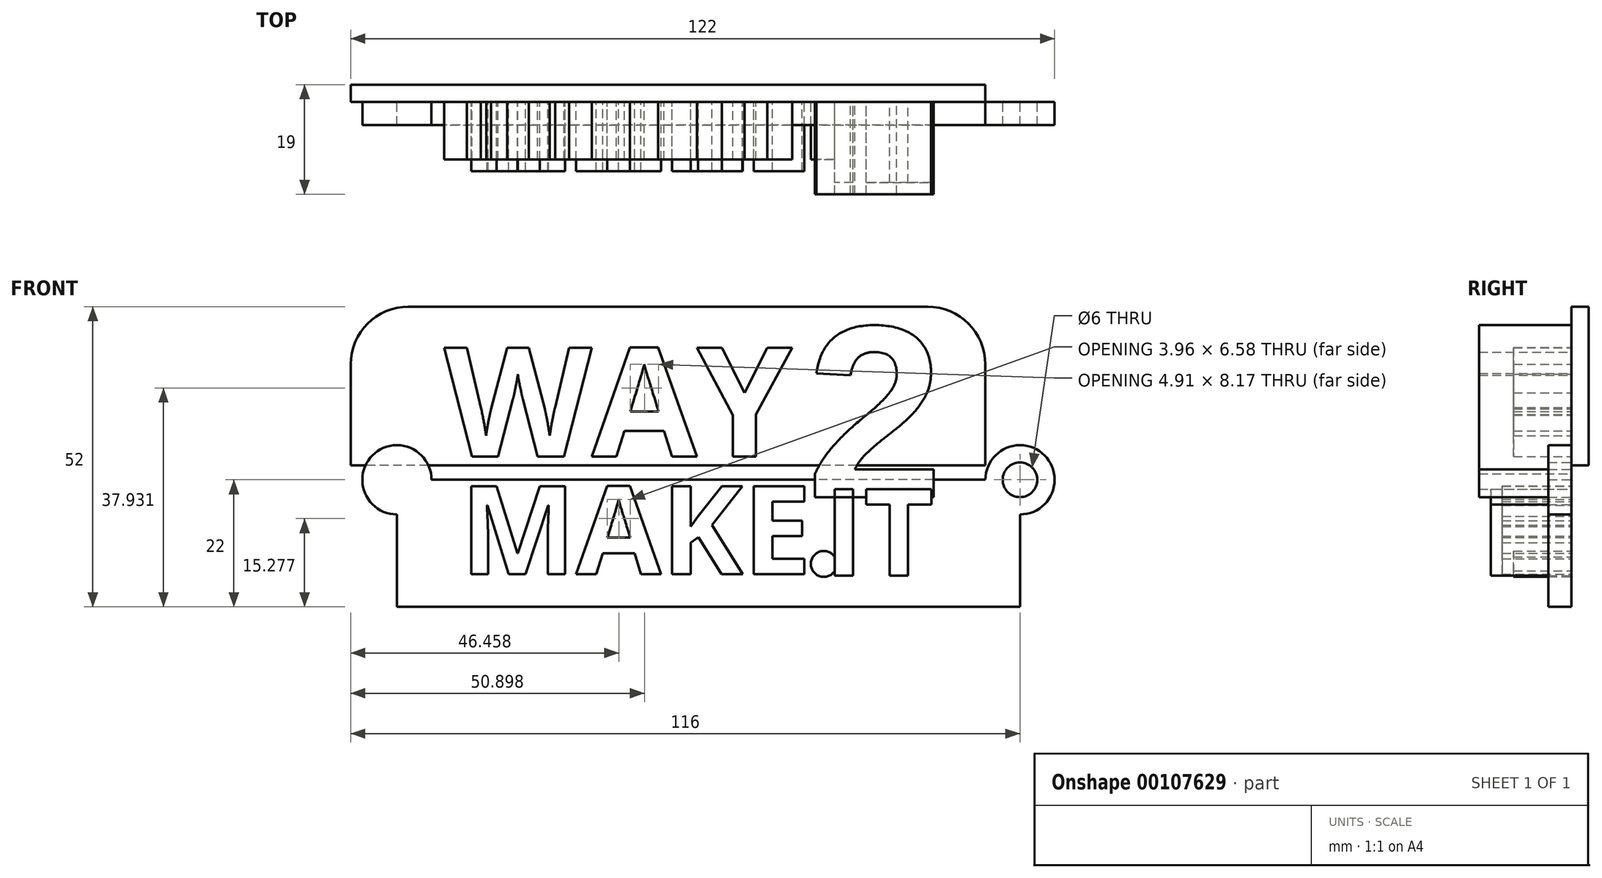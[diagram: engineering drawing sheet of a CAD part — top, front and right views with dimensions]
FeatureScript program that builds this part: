
annotation { "Feature Type Name" : "Feature", "Feature Type Description" : "" }
export const myFeature = defineFeature(function(context is Context, id is Id, definition is map)
    precondition{}
    {
        {
            var Q0;
            Q0=qCreatedBy(makeId("Front.planeOp"),FACE);
            var sketch = newSketch(context, id + "F0", { "sketchPlane" : qUnion([Q0])});
            skText(sketch, "E0", { "text": "WAY", "fontName": "OpenSans-Bold.ttf"});
            skText(sketch, "E1", { "text": "2", "fontName": "Arimo-Bold.ttf"});
            skText(sketch, "E2", { "text": "MAKE", "fontName": "OpenSans-Bold.ttf"});
            skText(sketch, "E3", { "text": "IT", "fontName": "OpenSans-Bold.ttf"});
            const initialGuessF0  = {"E0": [-0.0538, 0, 1, 0, 0.01903], "E1": [0.009, -0.007, 1, 0, 0.03074], "E2": [-0.051, -0.02034, 1, 0, 0.01534], "E3": [0.012, -0.02058, 1, 0, 0.01508]};
            skSetInitialGuess(sketch, initialGuessF0);
            skSolve(sketch);
        }
        {
            var Q0;
            Q0=makeQuery(id+"F0.imprint","IMPRINT",FACE,{"disambiguationData":[TD([[makeQuery(id+"F0.imprint","IMPRINT",EDGE,{"derivedFrom":sQuery(id+"F0.wireOp",EDGE,"E0.sketch_text.stroke-0")}),-1.0]])]});
            var Q1;
            Q1=makeQuery(id+"F0.imprint","IMPRINT",FACE,{"disambiguationData":[TD([[makeQuery(id+"F0.imprint","IMPRINT",EDGE,{"derivedFrom":sQuery(id+"F0.wireOp",EDGE,"E0.sketch_text.stroke-20")}),-1.0]])]});
            var Q2;
            Q2=makeQuery(id+"F0.imprint","IMPRINT",FACE,{"disambiguationData":[TD([[makeQuery(id+"F0.imprint","IMPRINT",EDGE,{"derivedFrom":sQuery(id+"F0.wireOp",EDGE,"E0.sketch_text.stroke-33")}),-1.0]])]});
            var Q3;
            Q3=makeQuery(id+"F0.imprint","IMPRINT",FACE,{"disambiguationData":[TD([[makeQuery(id+"F0.imprint","IMPRINT",EDGE,{"derivedFrom":sQuery(id+"F0.wireOp",EDGE,"E0.sketch_text.stroke-36")}),-1.0]])]});
            extrude(context, id + "F1", {"entities" : qUnion([Q0, Q1, Q2, Q3]), "depth" : 10 * mm});
        }
        {
            var Q0;
            {var subQ4=sQuery(id+"F0.wireOp",EDGE,"E1.sketch_text.stroke-0");Q0=makeQuery(id+"F0.imprint","IMPRINT",FACE,{"disambiguationData":[TD([[makeQuery(id+"F0.imprint","IMPRINT",EDGE,{"derivedFrom":subQ4}),-1.0]])]});}
            extrude(context, id + "F2", {"entities" : qUnion([Q0]), "depth" : 16 * mm});
        }
        {
            var Q0;
            Q0=makeQuery(id+"F0.imprint","IMPRINT",FACE,{"disambiguationData":[TD([[makeQuery(id+"F0.imprint","IMPRINT",EDGE,{"derivedFrom":sQuery(id+"F0.wireOp",EDGE,"E2.sketch_text.stroke-0")}),-1.0]])]});
            var Q1;
            Q1=makeQuery(id+"F0.imprint","IMPRINT",FACE,{"disambiguationData":[TD([[makeQuery(id+"F0.imprint","IMPRINT",EDGE,{"derivedFrom":sQuery(id+"F0.wireOp",EDGE,"E2.sketch_text.stroke-19")}),-1.0]])]});
            var Q2;
            Q2=makeQuery(id+"F0.imprint","IMPRINT",FACE,{"disambiguationData":[TD([[makeQuery(id+"F0.imprint","IMPRINT",EDGE,{"derivedFrom":sQuery(id+"F0.wireOp",EDGE,"E2.sketch_text.stroke-31")}),-1.0]])]});
            var Q3;
            Q3=makeQuery(id+"F0.imprint","IMPRINT",FACE,{"disambiguationData":[TD([[makeQuery(id+"F0.imprint","IMPRINT",EDGE,{"derivedFrom":sQuery(id+"F0.wireOp",EDGE,"E2.sketch_text.stroke-44")}),-1.0]])]});
            extrude(context, id + "F3", {"entities" : qUnion([Q0, Q1, Q2, Q3]), "depth" : 12 * mm});
        }
        {
            var Q0;
            {var subQ5=sQuery(id+"F0.wireOp",EDGE,"E3.sketch_text.stroke-11");Q0=makeQuery(id+"F0.imprint","IMPRINT",FACE,{"disambiguationData":[TD([[makeQuery(id+"F0.imprint","IMPRINT",EDGE,{"derivedFrom":subQ5}),-1.0]])]});}
            var Q1;
            {var subQ1=sQuery(id+"F0.wireOp",EDGE,"E3.sketch_text.stroke-12");Q1=makeQuery(id+"F0.imprint","IMPRINT",FACE,{"disambiguationData":[TD([[makeQuery(id+"F0.imprint","IMPRINT",EDGE,{"derivedFrom":subQ1}),-1.0]])]});}
            var Q2;
            {var subQ0=sQuery(id+"F0.wireOp",EDGE,"E3.sketch_text.stroke-14");Q2=makeQuery(id+"F0.imprint","IMPRINT",FACE,{"disambiguationData":[TD([[makeQuery(id+"F0.imprint","IMPRINT",EDGE,{"derivedFrom":subQ0}),-1.0]])]});}
            var Q3;
            {var subQ5=sQuery(id+"F0.wireOp",EDGE,"E3.sketch_text.stroke-3");Q3=makeQuery(id+"F0.imprint","IMPRINT",FACE,{"disambiguationData":[TD([[makeQuery(id+"F0.imprint","IMPRINT",EDGE,{"derivedFrom":subQ5}),-1.0]])]});}
            var Q4;
            {var subQ0=sQuery(id+"F0.wireOp",EDGE,"E3.sketch_text.stroke-6");Q4=makeQuery(id+"F0.imprint","IMPRINT",FACE,{"disambiguationData":[TD([[makeQuery(id+"F0.imprint","IMPRINT",EDGE,{"derivedFrom":subQ0}),-1.0]])]});}
            var Q5;
            {var subQ5=sQuery(id+"F0.wireOp",EDGE,"E3.sketch_text.stroke-9");Q5=makeQuery(id+"F0.imprint","IMPRINT",FACE,{"disambiguationData":[TD([[makeQuery(id+"F0.imprint","IMPRINT",EDGE,{"derivedFrom":subQ5}),-1.0]])]});}
            extrude(context, id + "F4", {"entities" : qUnion([Q0, Q1, Q2, Q3, Q4, Q5]), "depth" : 14 * mm});
        }
        {
            var Q0;
            Q0=qCreatedBy(makeId("Front.planeOp"),FACE);
            var sketch = newSketch(context, id + "F5", { "sketchPlane" : qUnion([Q0])});
            skCircle(sketch, "E4", {"center": v(12, -18.58) * mm, "radius": 2.25 * mm});
            skSolve(sketch);
        }
        {
            var Q0;
            Q0=makeQuery(id+"F5.imprint","IMPRINT",FACE,{"disambiguationData":[TD([[makeQuery(id+"F5.imprint","IMPRINT",EDGE,{"derivedFrom":sQuery(id+"F5.wireOp",EDGE,"E4")}),1.0]])]});
            extrude(context, id + "F6", {"entities" : qUnion([Q0]), "operationType" : NewBodyOperationType.ADD, "depth" : 10 * mm});
        }
        {
            var Q0;
            Q0=qCreatedBy(makeId("Right.planeOp"),FACE);
            var sketch = newSketch(context, id + "F7", { "sketchPlane" : qUnion([Q0])});
            skLineSegment(sketch, "E5.bottom", {"start": v(0, 0) * mm, "end": v(3, 0) * mm});
            skLineSegment(sketch, "E5.top", {"start": v(0, 26) * mm, "end": v(3, 26) * mm});
            skLineSegment(sketch, "E5.left", {"start": v(0, 0) * mm, "end": v(0, 26) * mm});
            skLineSegment(sketch, "E5.right", {"start": v(3, 0) * mm, "end": v(3, 26) * mm});
            skLineSegment(sketch, "E6.top", {"start": v(0, -1.47) * mm, "end": v(3, -1.47) * mm});
            skLineSegment(sketch, "E6.left", {"start": v(0, 0) * mm, "end": v(0, -1.47) * mm});
            skLineSegment(sketch, "E6.right", {"start": v(3, 0) * mm, "end": v(3, -1.47) * mm});
            skSolve(sketch);
        }
        {
            var Q0;
            Q0 = qSketchRegion(id + "F7", true);
            extrude(context, id + "F8", {"entities" : qUnion([Q0]), "depth" : 40 * mm, "hasSecondDirection" : true, "secondDirectionOppositeDirection" : true, "secondDirectionDepth" : 70 * mm});
        }
        {
            var Q0;
            Q0=qCreatedBy(makeId("Right.planeOp"),FACE);
            var sketch = newSketch(context, id + "F9", { "sketchPlane" : qUnion([Q0])});
            skLineSegment(sketch, "E7.bottom", {"start": v(0, -5) * mm, "end": v(3, -5) * mm});
            skLineSegment(sketch, "E7.top", {"start": v(0, -30) * mm, "end": v(3, -30) * mm});
            skLineSegment(sketch, "E7.left", {"start": v(0, -5) * mm, "end": v(0, -30) * mm});
            skLineSegment(sketch, "E7.right", {"start": v(3, -5) * mm, "end": v(3, -30) * mm});
            skLineSegment(sketch, "E8.top", {"start": v(0, -3.53) * mm, "end": v(3, -3.53) * mm});
            skLineSegment(sketch, "E8.left", {"start": v(0, -5) * mm, "end": v(0, -3.53) * mm});
            skLineSegment(sketch, "E8.right", {"start": v(3, -5) * mm, "end": v(3, -3.53) * mm});
            skSolve(sketch);
        }
        {
            var Q0;
            Q0=makeQuery(id+"Fe1C7CBQt6am3Dv_12.opExtrude","CAP_EDGE",EDGE,{"disambiguationData":[OSD([sQuery(id+"F9.wireOp",EDGE,"E7.top")])],"isStart":false});
            var Q1;
            Q1=makeQuery(id+"F8.opExtrude","CAP_EDGE",EDGE,{"disambiguationData":[OSD([sQuery(id+"F7.wireOp",EDGE,"E5.top")])],"isStart":false});
            var Q2;
            Q2=makeQuery(id+"F8.opExtrude","CAP_EDGE",EDGE,{"disambiguationData":[OSD([sQuery(id+"F7.wireOp",EDGE,"E5.top")])],"isStart":true});
            var Q3;
            Q3=makeQuery(id+"Fe1C7CBQt6am3Dv_12.opExtrude","CAP_EDGE",EDGE,{"disambiguationData":[OSD([sQuery(id+"F9.wireOp",EDGE,"E7.top")])],"isStart":true});
            fillet(context, id + "F10", {"entities" : qUnion([Q0, Q1, Q2, Q3]), "radius" : 10 * mm, "tangentPropagation" : true, "allowEdgeOverflow" : false});
        }
        {
            var Q0;
            Q0=makeQuery(id+"F8.opExtrude","SWEPT_FACE",FACE,{"disambiguationData":[OSD([sQuery(id+"F7.wireOp",EDGE,"E5.left")])]});
            var sketch = newSketch(context, id + "F11", { "sketchPlane" : qUnion([Q0])});
            skCircle(sketch, "E9", {"center": v(-64, 6) * mm, "radius": 2.5 * mm});
            skCircle(sketch, "E10", {"center": v(-64, -11) * mm, "radius": 2.5 * mm});
            skSolve(sketch);
        }
        {
            var Q0;
            Q0=makeQuery(id+"F8.opExtrude","SWEPT_FACE",FACE,{"disambiguationData":[OSD([sQuery(id+"F7.wireOp",EDGE,"E5.left"),sQuery(id+"F7.wireOp",EDGE,"E6.left")])]});
            var sketch = newSketch(context, id + "F12", { "sketchPlane" : qUnion([Q0])});
            skLineSegment(sketch, "E11", {"start": v(46, -4) * mm, "end": v(46, -26) * mm});
            skCircle(sketch, "E12", {"center": v(46, -4) * mm, "radius": 6 * mm});
            skLineSegment(sketch, "E13", {"start": v(46, -4) * mm, "end": v(-62, -4) * mm});
            skLineSegment(sketch, "E14", {"start": v(-62, -4) * mm, "end": v(-62, -26) * mm});
            skLineSegment(sketch, "E15", {"start": v(-62, -26) * mm, "end": v(46, -26) * mm});
            skCircle(sketch, "E16", {"center": v(-62, -4) * mm, "radius": 6 * mm});
            skCircle(sketch, "E17", {"center": v(46, -4) * mm, "radius": 3 * mm});
            skSolve(sketch);
        }
        {
            var Q0;
            {var subQ0=sQuery(id+"F12.wireOp",EDGE,"E15");Q0=makeQuery(id+"F12.imprint","IMPRINT",FACE,{"disambiguationData":[TD([[makeQuery(id+"F12.imprint","IMPRINT",EDGE,{"derivedFrom":subQ0}),1.0]])]});}
            var Q1;
            {var subQ0=sQuery(id+"F12.wireOp",EDGE,"E14");var subQ1=sQuery(id+"F12.wireOp",EDGE,"E13");var subQ2=makeQuery(id+"F12.imprint","INTERSECT",VERTEX,{"derivedFrom":[subQ1,subQ0]});Q1=makeQuery(id+"F12.imprint","IMPRINT",FACE,{"disambiguationData":[TD([[makeQuery(id+"F12.imprint","IMPRINT",EDGE,{"disambiguationData":[TD([[subQ2,1.0]])],"derivedFrom":subQ1}),1.0]])]});}
            var Q2;
            {var subQ1=sQuery(id+"F12.wireOp",EDGE,"E13");var subQ5=sQuery(id+"F12.wireOp",EDGE,"E14");var subQ8=makeQuery(id+"F12.imprint","INTERSECT",VERTEX,{"derivedFrom":[subQ1,subQ5]});Q2=makeQuery(id+"F12.imprint","IMPRINT",FACE,{"disambiguationData":[TD([[makeQuery(id+"F12.imprint","IMPRINT",EDGE,{"disambiguationData":[TD([[subQ8,1.0]])],"derivedFrom":subQ1}),-1.0]])]});}
            var Q3;
            {var subQ0=sQuery(id+"F12.wireOp",EDGE,"E16");var subQ1=makeQuery(id+"F8.opExtrude","SWEPT_EDGE",EDGE,{"disambiguationData":[OSD([sQuery(id+"F7.wireOp",EDGE,"E6.top"),sQuery(id+"F7.wireOp",EDGE,"E6.left")])]});var subQ2=makeQuery(id+"F12.imprint","INTERSECT",VERTEX,{"disambiguationData":[OD(0.0)],"derivedFrom":[subQ1,subQ0]});Q3=makeQuery(id+"F12.imprint","IMPRINT",FACE,{"disambiguationData":[TD([[makeQuery(id+"F12.imprint","IMPRINT",EDGE,{"disambiguationData":[TD([[subQ2,-1.0]])],"derivedFrom":subQ0}),1.0]])]});}
            var Q4;
            {var subQ0=sQuery(id+"F12.wireOp",EDGE,"E12");var subQ1=sQuery(id+"F12.wireOp",EDGE,"E11");var subQ2=makeQuery(id+"F12.imprint","INTERSECT",VERTEX,{"derivedFrom":[subQ1,subQ0]});Q4=makeQuery(id+"F12.imprint","IMPRINT",FACE,{"disambiguationData":[TD([[makeQuery(id+"F12.imprint","IMPRINT",EDGE,{"disambiguationData":[TD([[subQ2,1.0]])],"derivedFrom":subQ1}),1.0]])]});}
            var Q5;
            {var subQ0=sQuery(id+"F12.wireOp",EDGE,"E12");var subQ1=sQuery(id+"F12.wireOp",EDGE,"E11");var subQ2=makeQuery(id+"F12.imprint","INTERSECT",VERTEX,{"derivedFrom":[subQ1,subQ0]});Q5=makeQuery(id+"F12.imprint","IMPRINT",FACE,{"disambiguationData":[TD([[makeQuery(id+"F12.imprint","IMPRINT",EDGE,{"disambiguationData":[TD([[subQ2,1.0]])],"derivedFrom":subQ1}),-1.0]])]});}
            extrude(context, id + "F13", {"entities" : qUnion([Q0, Q1, Q2, Q3, Q4, Q5]), "depth" : 4 * mm, "offsetDistance" : 25 * mm});
        }
    });
